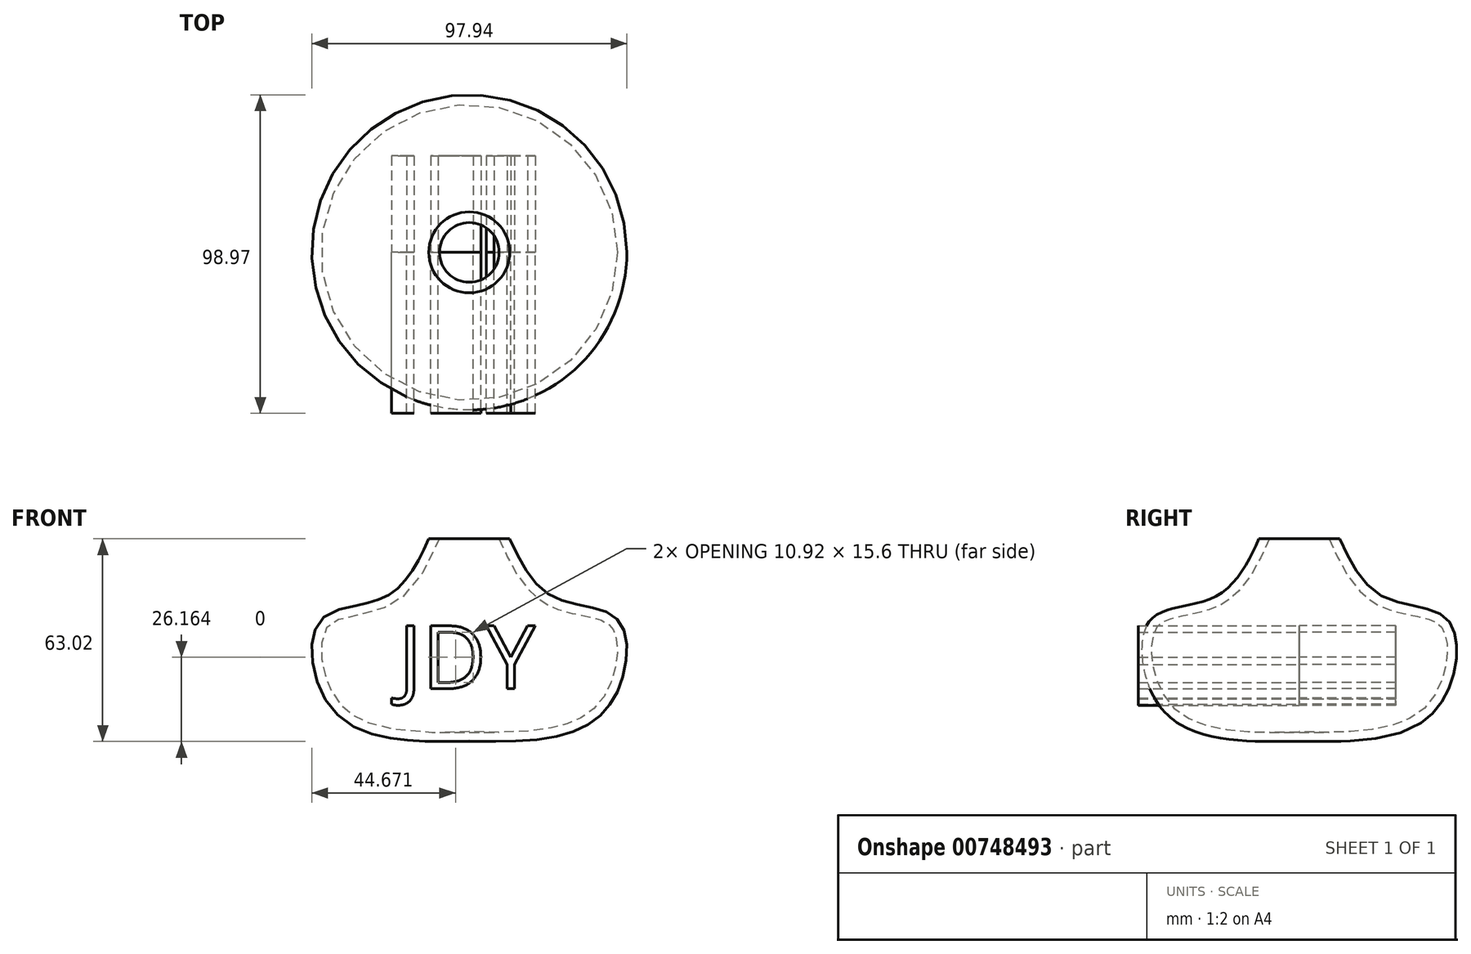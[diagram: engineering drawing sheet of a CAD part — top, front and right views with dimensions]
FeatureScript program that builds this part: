
annotation { "Feature Type Name" : "Feature", "Feature Type Description" : "" }
export const myFeature = defineFeature(function(context is Context, id is Id, definition is map)
    precondition{}
    {
        {
            var Q0;
            Q0=qCreatedBy(makeId("Front.planeOp"),FACE);
            var sketch = newSketch(context, id + "F0", { "sketchPlane" : qUnion([Q0])});
            skFitSpline(sketch, "E0", {"points": [v(10.62, 34.46) * mm, v(25.99, 12) * mm, v(45.84, 5.15) * mm, v(47.02, -15.18) * mm, v(32.13, -30.07) * mm, v(-14.43, -32.2) * mm], "startDerivative": vector(59.06, -137.55) * mm, "endDerivative": vector(-199.4, 10.96) * mm});
            skFitSpline(sketch, "E1.0", {"points": [v(7.87, 33.27) * mm, v(8.48, 31.84) * mm, v(9.72, 28.95) * mm, v(11.69, 24.67) * mm, v(13.85, 20.55) * mm, v(16.3, 16.7) * mm, v(18.7, 13.83) * mm, v(20.89, 11.8) * mm, v(22.38, 10.67) * mm, v(23.65, 9.86) * mm, v(24.64, 9.3) * mm, v(25.66, 8.82) * mm, v(27.04, 8.24) * mm, v(28.77, 7.65) * mm, v(31.54, 6.9) * mm, v(34.91, 6.22) * mm, v(37.97, 5.59) * mm, v(40.09, 5) * mm, v(41.47, 4.5) * mm, v(42.6, 3.92) * mm, v(43.26, 3.45) * mm, v(43.63, 3.11) * mm, v(43.86, 2.88) * mm, v(44.14, 2.57) * mm, v(44.45, 2.13) * mm, v(44.83, 1.48) * mm, v(45.24, 0.53) * mm, v(45.63, -0.83) * mm, v(45.88, -2.36) * mm, v(46.02, -4.58) * mm, v(45.85, -7.62) * mm, v(45.26, -10.73) * mm, v(44.57, -13.13) * mm, v(43.76, -15.42) * mm, v(42.54, -18) * mm, v(40.75, -20.68) * mm, v(38.6, -22.99) * mm, v(36.02, -24.96) * mm, v(33.47, -26.32) * mm, v(31.17, -27.25) * mm, v(28.67, -28.06) * mm, v(25.17, -28.87) * mm, v(18.9, -29.76) * mm, v(10, -30.17) * mm, v(-1.83, -29.88) * mm, v(-10.11, -29.43) * mm, v(-14.27, -29.2) * mm]});
            skLineSegment(sketch, "E2", {"start": v(-5.69, 29.97) * mm, "end": v(37.1, 29.97) * mm});
            skPoint(sketch, "E3.start.orphan", {"position": v(0, 16.5) * mm});
            skLineSegment(sketch, "E4", {"start": v(0, 36.97) * mm, "end": v(0, -37.66) * mm});
            skSolve(sketch);
        }
        {
            var Q0;
            {var subQ0=sQuery(id+"F0.wireOp",EDGE,"E2");var subQ1=sQuery(id+"F0.wireOp",EDGE,"E0");var subQ2=makeQuery(id+"F0.imprint","INTERSECT",VERTEX,{"derivedFrom":[subQ1,subQ0]});Q0=makeQuery(id+"F0.imprint","IMPRINT",FACE,{"disambiguationData":[TD([[makeQuery(id+"F0.imprint","IMPRINT",EDGE,{"disambiguationData":[TD([[subQ2,-1.0]])],"derivedFrom":subQ1}),-1.0]])]});}
            var Q1;
            Q1=sQuery(id+"F0.wireOp",EDGE,"E4");
            revolve(context, id + "F1", {"surfaceOperationType" : NewSurfaceOperationType.NEW, "entities" : qUnion([Q0]), "axis" : qUnion([Q1]), "revolveType" : RevolveType.FULL});
        }
        {
            var Q0;
            Q0=qCreatedBy(makeId("Front.planeOp"),FACE);
            var sketch = newSketch(context, id + "F2", { "sketchPlane" : qUnion([Q0])});
            skText(sketch, "E5", { "text": "JDY", "fontName": "OpenSans-Regular.ttf"});
            const initialGuessF2  = {"E5": [-0.02202, -0.01665, 1, 0, 0.0197]};
            skSetInitialGuess(sketch, initialGuessF2);
            skSolve(sketch);
        }
        {
            var Q0;
            Q0 = qSketchRegion(id + "F2", true);
            extrude(context, id + "F3", {"entities" : qUnion([Q0]), "oppositeDirection" : true, "depth" : 30 * mm, "offsetDistance" : 25 * mm});
        }
        {
            var Q0;
            Q0 = qSketchRegion(id + "F2", true);
            extrude(context, id + "F4", {"entities" : qUnion([Q0]), "depth" : 50 * mm, "offsetDistance" : 25 * mm});
        }
    });
